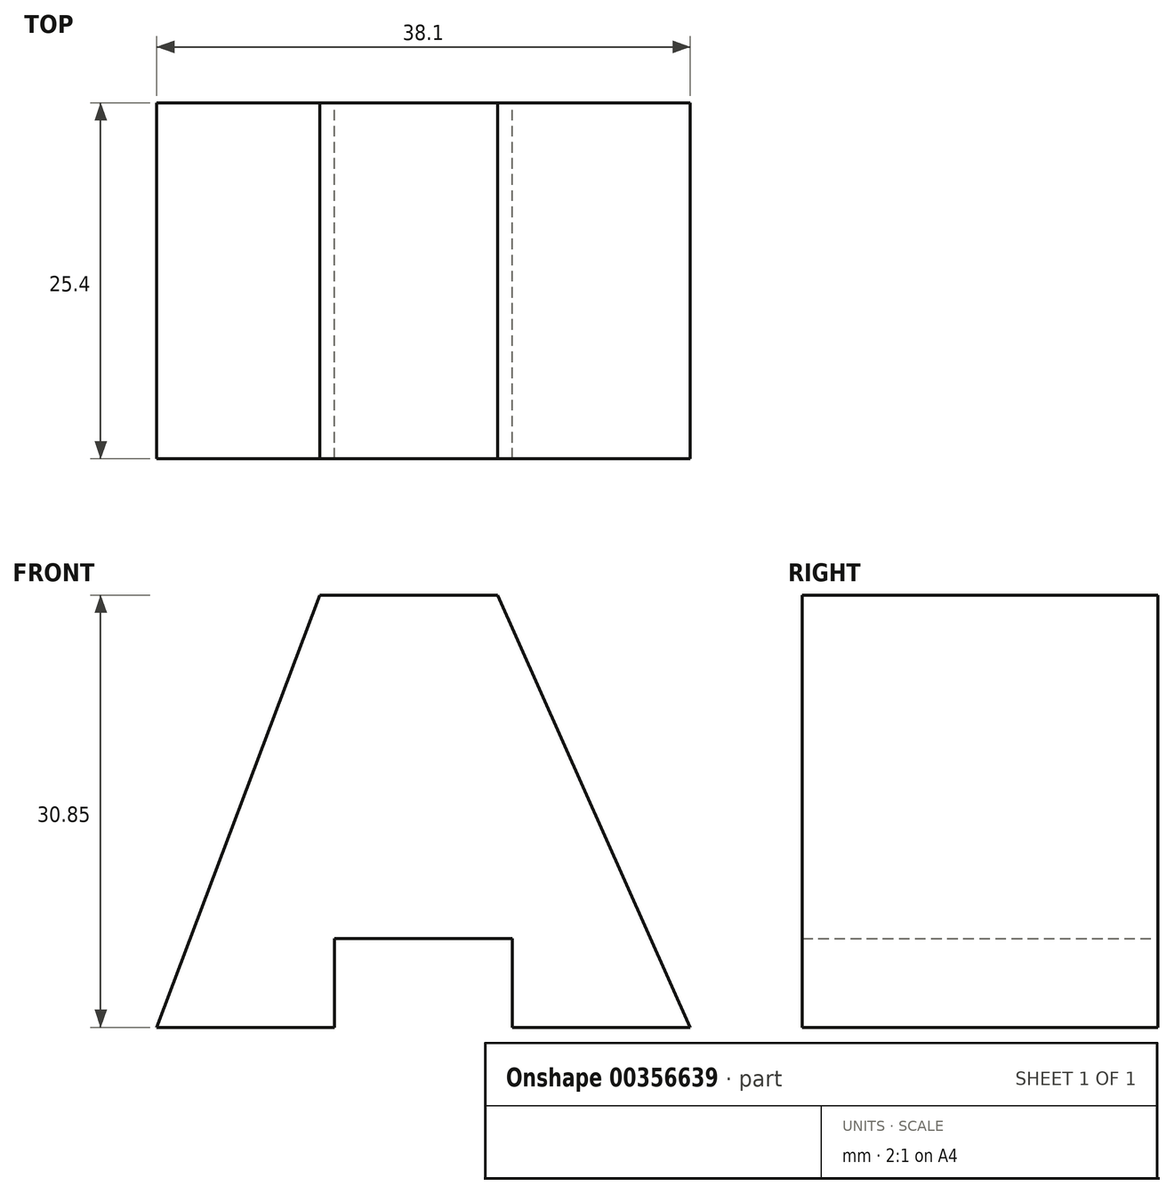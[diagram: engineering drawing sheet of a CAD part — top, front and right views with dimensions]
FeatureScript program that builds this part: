
annotation { "Feature Type Name" : "Feature", "Feature Type Description" : "" }
export const myFeature = defineFeature(function(context is Context, id is Id, definition is map)
    precondition{}
    {
        {
            var Q0;
            Q0=qCreatedBy(makeId("Front.planeOp"),FACE);
            var sketch = newSketch(context, id + "F0", { "sketchPlane" : qUnion([Q0])});
            skLineSegment(sketch, "E0", {"start": v(-20.52, 30.85) * mm, "end": v(-7.82, 30.85) * mm});
            skLineSegment(sketch, "E1", {"start": v(-7.82, 30.85) * mm, "end": v(5.94, 0) * mm});
            skLineSegment(sketch, "E2", {"start": v(-32.16, 0) * mm, "end": v(-20.52, 30.85) * mm});
            skLineSegment(sketch, "E3", {"start": v(-32.16, 0) * mm, "end": v(5.94, 0) * mm});
            skSolve(sketch);
        }
        {
            var Q0;
            Q0 = qSketchRegion(id + "F0", true);
            extrude(context, id + "F1", {"entities" : qUnion([Q0]), "depth" : 25.4 * mm});
        }
        {
            var Q0;
            Q0=qCreatedBy(makeId("Front.planeOp"),FACE);
            var sketch = newSketch(context, id + "F2", { "sketchPlane" : qUnion([Q0])});
            skLineSegment(sketch, "E4", {"start": v(-19.46, 0) * mm, "end": v(-19.46, 6.35) * mm});
            skLineSegment(sketch, "E5", {"start": v(-19.46, 6.35) * mm, "end": v(-6.76, 6.35) * mm});
            skLineSegment(sketch, "E6", {"start": v(-6.76, 6.35) * mm, "end": v(-6.76, 0) * mm});
            skLineSegment(sketch, "E7", {"start": v(-19.46, 0) * mm, "end": v(-6.76, 0) * mm});
            skSolve(sketch);
        }
        {
            var Q0;
            Q0 = qSketchRegion(id + "F2", true);
            extrude(context, id + "F3", {"entities" : qUnion([Q0]), "operationType" : NewBodyOperationType.REMOVE, "depth" : 31.75 * mm});
        }
    });
